# Revit family: KLVL176NB
name_source: partatom
category: Lighting Fixtures
revit_build: Autodesk Revit 2014 (Build: 20130308_1515(x64)
units: mm (PartAtom-declared; Revit-internal decimal feet)

## types (2) — shared parameters
Assembly Code = D5020200
Color Filter = 16777215
Description = Ravenna Highlighter is highly adaptable to landscape path lighting solutions. Elegance and style in leaf-like design blends into natural surroundings.
Diameter = 5 "
Dimming Lamp Color Temperature Shift = <None>
Glass = Glass-KIM-Temper Molded
Height = 24 "
Lamp = LED
Load Classification = Lighting
Manufacturer = Kim Lighting
MasterFormat Title = Landscape Lighting, Site Lighting, Walkway Lighting
Model = Ravenna Highlighter
Number of Poles = 1
Photometric Notes = More IES files download on Photometric Web Link
Photometric Web File = klvl171-3l3k.ies
Photometric Web Link = https://www.hubbell.com
Power Factor = 1
Product Documentation Link = https://hubbellcdn.com
Product Page URL = https://www.hubbell.com
Series = Landscape
Tilt Angle = 90.00°
Type Comments = landscape path light
URL = https://www.hubbell.com
Voltage = 120 V
Wattage Comments = default
Width = 5.31 "

## per-type parameters (varying)
| type | Apparent Load | Finish |
| BNL176NB | 10 VA | Metal-Hubbell-Brass |
| BNL176VG | 0 VA | Paint - Hubbell - Green Textured |

## geometry (parser evidence)
native form markers: Sweep x6
no freeform markers — native parametric forms only
